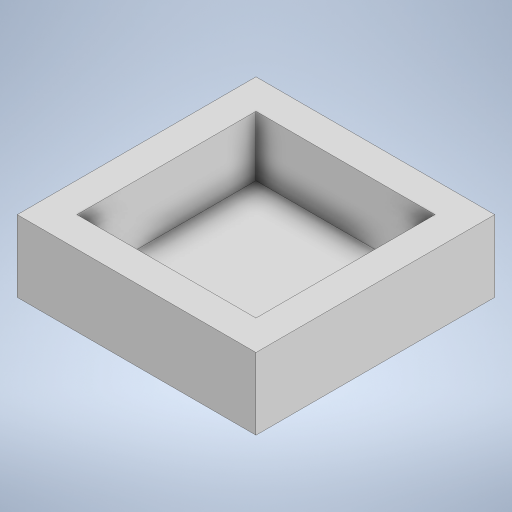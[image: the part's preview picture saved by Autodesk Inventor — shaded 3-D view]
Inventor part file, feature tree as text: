
AUTODESK INVENTOR PART (.ipt)
format: ipt  version: 2024.3 (Build 283343000, 343)  size: 211,456 bytes
history: native  units: in
note: dims shown in document units (in); Inventor stores cm internally (conversion verified against a paired STEP export)
features: extrude x2, sketch x2
ambient origin geometry x8: Origin, YZ Plane, XZ Plane, XY Plane, X Axis, Y Axis, Z Axis, Center Point
bodies: Solid1 (feature_tree)
feature tree (4):
  extrude  "Extrusion1"  Depth=2.3622in TaperAngle=0.0deg
  extrude  "Extrusion2"  Depth=1.9843in TaperAngle=0.0deg
  sketch  "Sketch1"  dims[d0=7.874in d1=2.3622in d2=0.0in]
  sketch  "Sketch2"  dims[d3=5.9055in d4=1.9843in d5=0.0in]
